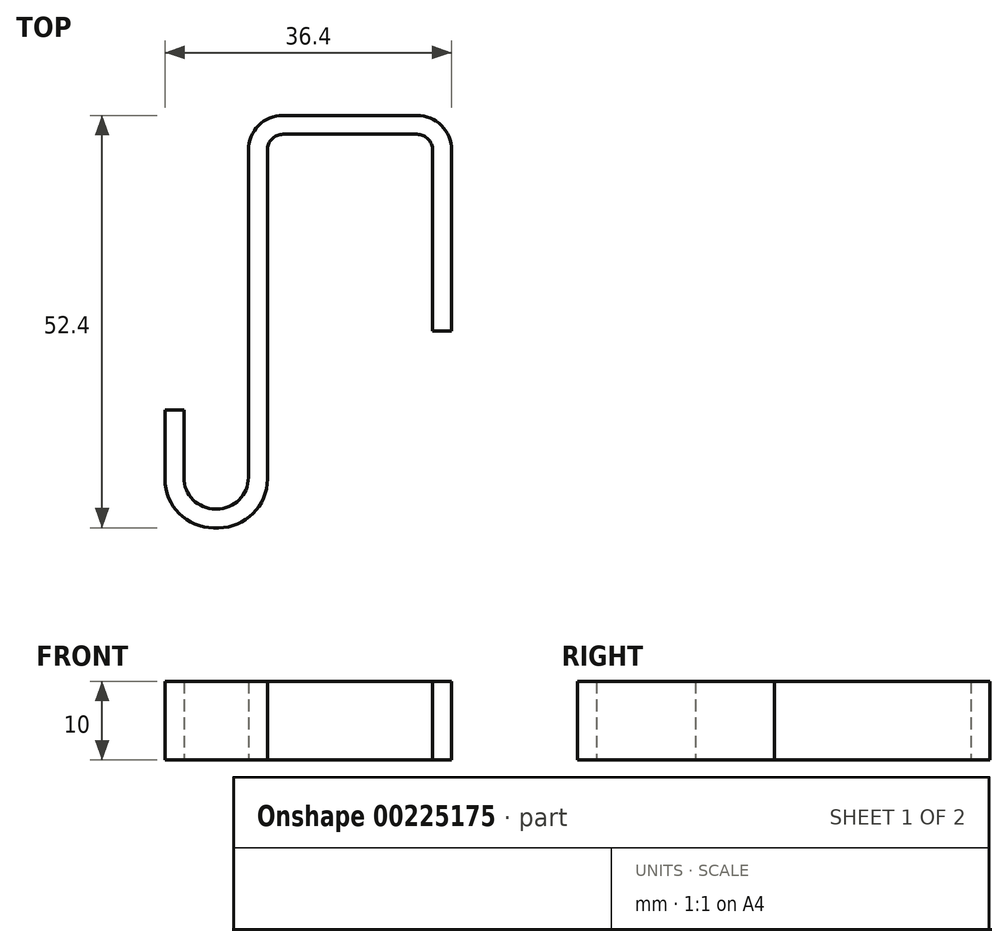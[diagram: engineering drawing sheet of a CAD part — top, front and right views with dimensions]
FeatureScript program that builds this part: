
annotation { "Feature Type Name" : "Feature", "Feature Type Description" : "" }
export const myFeature = defineFeature(function(context is Context, id is Id, definition is map)
    precondition{}
    {
        {
            var Q0;
            Q0=qCreatedBy(makeId("Top.planeOp"),FACE);
            var sketch = newSketch(context, id + "F0", { "sketchPlane" : qUnion([Q0])});
            skLineSegment(sketch, "E0", {"start": v(6.79, 2.7) * mm, "end": v(6.79, 27.7) * mm});
            skLineSegment(sketch, "E1", {"start": v(6.79, 27.7) * mm, "end": v(-14.21, 27.7) * mm});
            skLineSegment(sketch, "E2", {"start": v(-14.21, 27.7) * mm, "end": v(-14.21, -22.3) * mm});
            skLineSegment(sketch, "E3", {"start": v(-14.21, -22.3) * mm, "end": v(-27.21, -22.3) * mm});
            skLineSegment(sketch, "E4", {"start": v(-27.21, -22.3) * mm, "end": v(-27.21, -7.3) * mm});
            skLineSegment(sketch, "E5.0", {"start": v(-24.81, -19.9) * mm, "end": v(-24.81, -7.3) * mm});
            skLineSegment(sketch, "E5.1", {"start": v(9.19, 2.7) * mm, "end": v(9.19, 30.1) * mm});
            skLineSegment(sketch, "E5.2", {"start": v(9.19, 30.1) * mm, "end": v(-16.61, 30.1) * mm});
            skLineSegment(sketch, "E5.3", {"start": v(-16.61, 30.1) * mm, "end": v(-16.61, -19.9) * mm});
            skLineSegment(sketch, "E5.4", {"start": v(-16.61, -19.9) * mm, "end": v(-24.81, -19.9) * mm});
            skLineSegment(sketch, "E6", {"start": v(-24.81, -7.3) * mm, "end": v(-27.21, -7.3) * mm});
            skLineSegment(sketch, "E7", {"start": v(6.79, 2.7) * mm, "end": v(9.19, 2.7) * mm});
            skSolve(sketch);
        }
        {
            var Q0;
            Q0 = qSketchRegion(id + "F0", true);
            extrude(context, id + "F1", {"entities" : qUnion([Q0]), "depth" : 10 * mm});
        }
        {
            var Q0;
            Q0=makeQuery(id+"F1.opExtrude","SWEPT_EDGE",EDGE,{"disambiguationData":[OSD([sQuery(id+"F0.wireOp",EDGE,"E1"),sQuery(id+"F0.wireOp",EDGE,"E2")])]});
            var Q1;
            Q1=makeQuery(id+"F1.opExtrude","SWEPT_EDGE",EDGE,{"disambiguationData":[OSD([sQuery(id+"F0.wireOp",EDGE,"E0"),sQuery(id+"F0.wireOp",EDGE,"E1")])]});
            fillet(context, id + "F2", {"entities" : qUnion([Q0, Q1]), "radius" : 2 * mm, "tangentPropagation" : true, "allowEdgeOverflow" : false});
        }
        {
            var Q0;
            Q0=makeQuery(id+"F1.opExtrude","SWEPT_EDGE",EDGE,{"disambiguationData":[OSD([sQuery(id+"F0.wireOp",EDGE,"E5.2"),sQuery(id+"F0.wireOp",EDGE,"E5.3")])]});
            var Q1;
            Q1=makeQuery(id+"F1.opExtrude","SWEPT_EDGE",EDGE,{"disambiguationData":[OSD([sQuery(id+"F0.wireOp",EDGE,"E5.1"),sQuery(id+"F0.wireOp",EDGE,"E5.2")])]});
            fillet(context, id + "F3", {"entities" : qUnion([Q0, Q1]), "radius" : (2 + 2.4) * mm, "tangentPropagation" : true, "allowEdgeOverflow" : false});
        }
        {
            var Q0;
            Q0=makeQuery(id+"F1.opExtrude","SWEPT_EDGE",EDGE,{"disambiguationData":[OSD([sQuery(id+"F0.wireOp",EDGE,"E5.0"),sQuery(id+"F0.wireOp",EDGE,"E5.4")])]});
            var Q1;
            Q1=makeQuery(id+"F1.opExtrude","SWEPT_EDGE",EDGE,{"disambiguationData":[OSD([sQuery(id+"F0.wireOp",EDGE,"E5.3"),sQuery(id+"F0.wireOp",EDGE,"E5.4")])]});
            fillet(context, id + "F4", {"entities" : qUnion([Q0, Q1]), "radius" : 4 * mm, "tangentPropagation" : true, "allowEdgeOverflow" : false});
        }
        {
            var Q0;
            Q0=makeQuery(id+"F1.opExtrude","SWEPT_EDGE",EDGE,{"disambiguationData":[OSD([sQuery(id+"F0.wireOp",EDGE,"E3"),sQuery(id+"F0.wireOp",EDGE,"E4")])]});
            var Q1;
            Q1=makeQuery(id+"F1.opExtrude","SWEPT_EDGE",EDGE,{"disambiguationData":[OSD([sQuery(id+"F0.wireOp",EDGE,"E2"),sQuery(id+"F0.wireOp",EDGE,"E3")])]});
            fillet(context, id + "F5", {"entities" : qUnion([Q0, Q1]), "radius" : (5 + 1.2) * mm, "tangentPropagation" : true, "allowEdgeOverflow" : false});
        }
    });
